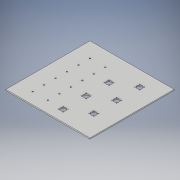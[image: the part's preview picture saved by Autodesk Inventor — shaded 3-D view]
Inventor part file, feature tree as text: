
AUTODESK INVENTOR PART (.ipt)
format: ipt  version: 2017 (Build 210142000, 142)  size: 207,360 bytes
history: native  units: in
note: dims shown in document units (in); Inventor stores cm internally (conversion verified against a paired STEP export)
features: extrude x1
ambient origin geometry x8: Origin, YZ Plane, XZ Plane, XY Plane, X Axis, Y Axis, Z Axis, Center Point
bodies: Body1 (feature_tree)
feature tree (1):
  extrude  "Extrusion5"  Depth=17.3228in
